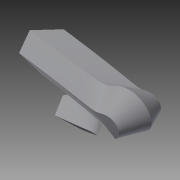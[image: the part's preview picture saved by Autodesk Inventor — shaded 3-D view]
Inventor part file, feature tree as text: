
AUTODESK INVENTOR PART (.ipt)
format: ipt  version: 2015 (Build 190159000, 159)  size: 270,336 bytes
history: native  units: in
note: dims shown in document units (in); Inventor stores cm internally (conversion verified against a paired STEP export)
features: sketch x2, sweep x1
ambient origin geometry x8: Origin, YZ Plane, XZ Plane, XY Plane, X Axis, Y Axis, Z Axis, Center Point
bodies: Solid1 (feature_tree)
feature tree (3):
  sweep  "Sweep1"
  sketch  "Sketch1"  dims[d0=0.0in d1=0.0in]
  sketch  "Sketch2"
